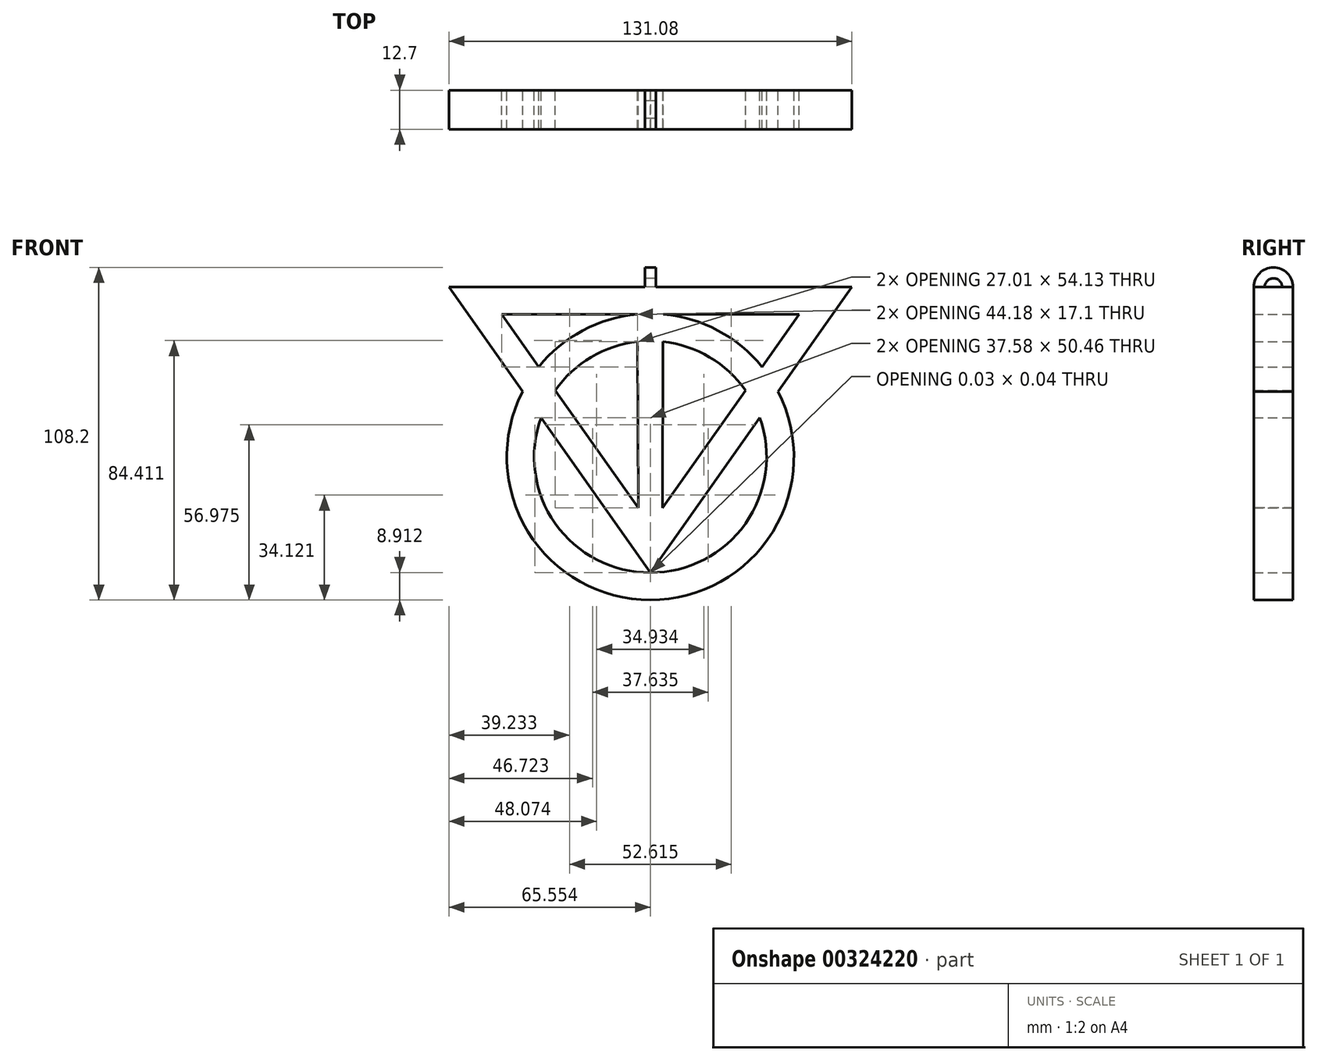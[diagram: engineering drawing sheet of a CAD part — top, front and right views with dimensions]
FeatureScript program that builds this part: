
annotation { "Feature Type Name" : "Feature", "Feature Type Description" : "" }
export const myFeature = defineFeature(function(context is Context, id is Id, definition is map)
    precondition{}
    {
        {
            var Q0;
            Q0=qCreatedBy(makeId("Front.planeOp"),FACE);
            var sketch = newSketch(context, id + "F0", { "sketchPlane" : qUnion([Q0])});
            skLineSegment(sketch, "E0", {"start": v(0.92, -47.6) * mm, "end": v(0.9, -47.56) * mm});
            skArc(sketch, "E1.trimOffspring", {"start": v(-2.73, 27.57) * mm, "mid": v(-2.98, 27.55) * mm, "end": v(-3.24, 27.52) * mm});
            skLineSegment(sketch, "E2.0", {"start": v(-2.9, -26.56) * mm, "end": v(-3.07, -26.3) * mm});
            skLineSegment(sketch, "E3.MirrorCS", {"start": v(0.92, -47.6) * mm, "end": v(36.48, 2.86) * mm});
            skLineSegment(sketch, "E4.MirrorCS", {"start": v(31.86, 11.74) * mm, "end": v(31.86, 11.74) * mm});
            skLineSegment(sketch, "E5.MirrorCS", {"start": v(37.24, 19.37) * mm, "end": v(49.29, 36.47) * mm});
            skLineSegment(sketch, "E6.trimOffspring", {"start": v(4.85, -26.58) * mm, "end": v(31.86, 11.74) * mm});
            skPoint(sketch, "E7.orphan", {"position": v(0.96, -32.1) * mm});
            skArc(sketch, "E8.trimOffspring", {"start": v(36.48, 2.86) * mm, "mid": v(31.83, -31.62) * mm, "end": v(0.92, -47.6) * mm});
            skArc(sketch, "E9.trimOffspring", {"start": v(0.86, -47.6) * mm, "mid": v(0.9, -47.6) * mm, "end": v(0.92, -47.6) * mm});
            skArc(sketch, "E10.0", {"start": v(0.86, -56.49) * mm, "mid": v(0.87, -56.49) * mm, "end": v(0.9, -56.49) * mm});
            skArc(sketch, "E11.0", {"start": v(42.46, 11.35) * mm, "mid": v(40.74, -34.25) * mm, "end": v(0.9, -56.49) * mm});
            skArc(sketch, "E12.0", {"start": v(5.1, 36.47) * mm, "mid": v(22.91, 31.19) * mm, "end": v(37.24, 19.37) * mm});
            skPoint(sketch, "E13.center.orphan", {"position": v(0.92, 32.3) * mm});
            skLineSegment(sketch, "E14", {"start": v(49.29, 36.47) * mm, "end": v(5.1, 36.47) * mm});
            skLineSegment(sketch, "E15.0", {"start": v(66.43, 45.36) * mm, "end": v(0.9, 45.36) * mm});
            skArc(sketch, "E16.0", {"start": v(5.02, 27.55) * mm, "mid": v(20.15, 22.55) * mm, "end": v(31.86, 11.74) * mm});
            skLineSegment(sketch, "E17", {"start": v(4.85, -26.58) * mm, "end": v(5.02, 27.55) * mm});
            skLineSegment(sketch, "E18.trimOffspring", {"start": v(42.46, 11.35) * mm, "end": v(66.43, 45.36) * mm});
            skLineSegment(sketch, "E19.trimOffspring", {"start": v(-3.04, 36.47) * mm, "end": v(-3.33, 36.47) * mm});
            skLineSegment(sketch, "E20", {"start": v(0.9, -47.6) * mm, "end": v(0.9, -47.56) * mm});
            skLineSegment(sketch, "E21.MirrorCS", {"start": v(-47.5, 36.47) * mm, "end": v(-46.74, 36.47) * mm});
            skLineSegment(sketch, "E22.MirrorCS", {"start": v(-3.07, -26.58) * mm, "end": v(-3.07, -26.3) * mm});
            skLineSegment(sketch, "E23.trimOffspring", {"start": v(0.9, 45.36) * mm, "end": v(65.54, 45.36) * mm});
            skPoint(sketch, "E24.MirrorCS.end.orphan", {"position": v(-3.07, -26.58) * mm});
            skPoint(sketch, "E24.MirrorCS.start.orphan", {"position": v(-30.08, 11.74) * mm});
            skPoint(sketch, "E25.MirrorCS.end.orphan", {"position": v(-64.65, 45.36) * mm});
            skPoint(sketch, "E25.MirrorCS.start.orphan", {"position": v(-40.68, 11.35) * mm});
            skPoint(sketch, "E26.MirrorCS.end.orphan", {"position": v(-63.76, 45.36) * mm});
            skPoint(sketch, "E27.orphan", {"position": v(-3.33, 36.47) * mm});
            skPoint(sketch, "E28.MirrorCS.start.orphan", {"position": v(-3.24, 27.55) * mm});
            skPoint(sketch, "E29.MirrorCS.start.orphan", {"position": v(-34.7, 2.86) * mm});
            skLineSegment(sketch, "E30.trimOffspring", {"start": v(-3.24, 27.52) * mm, "end": v(-3.24, 27.55) * mm});
            skArc(sketch, "E31.MirrorCS", {"start": v(-34.7, 2.86) * mm, "mid": v(-30.05, -31.62) * mm, "end": v(0.86, -47.6) * mm});
            skLineSegment(sketch, "E32.MirrorCS", {"start": v(0.86, -47.6) * mm, "end": v(-34.7, 2.86) * mm});
            skArc(sketch, "E33.MirrorCS", {"start": v(-40.68, 11.35) * mm, "mid": v(-38.96, -34.25) * mm, "end": v(0.9, -56.49) * mm});
            skLineSegment(sketch, "E34.MirrorCS", {"start": v(-3.07, -26.58) * mm, "end": v(-30.08, 11.74) * mm});
            skArc(sketch, "E35.MirrorCS", {"start": v(-3.24, 27.55) * mm, "mid": v(-18.37, 22.55) * mm, "end": v(-30.08, 11.74) * mm});
            skLineSegment(sketch, "E36.MirrorCS", {"start": v(-3.07, -26.58) * mm, "end": v(-3.24, 27.55) * mm});
            skArc(sketch, "E37.MirrorCS", {"start": v(-3.33, 36.47) * mm, "mid": v(-21.13, 31.19) * mm, "end": v(-35.45, 19.37) * mm});
            skLineSegment(sketch, "E38.MirrorCS", {"start": v(0.9, 45.36) * mm, "end": v(-64.65, 45.36) * mm});
            skLineSegment(sketch, "E39.MirrorCS", {"start": v(-40.68, 11.35) * mm, "end": v(-64.65, 45.36) * mm});
            skLineSegment(sketch, "E40.MirrorCS", {"start": v(-47.5, 36.47) * mm, "end": v(-3.33, 36.47) * mm});
            skLineSegment(sketch, "E41.MirrorCS", {"start": v(-35.45, 19.37) * mm, "end": v(-47.5, 36.47) * mm});
            skSolve(sketch);
        }
        {
            var Q0;
            {var subQ13=sQuery(id+"F0.wireOp",EDGE,"E0");Q0=makeQuery(id+"F0.imprint","IMPRINT",FACE,{"disambiguationData":[TD([[makeQuery(id+"F0.imprint","IMPRINT",EDGE,{"derivedFrom":subQ13}),-1.0]])]});}
            extrude(context, id + "F1", {"entities" : qUnion([Q0]), "depth" : 12.7 * mm});
        }
        {
            var Q0;
            Q0=makeQuery(id+"F1.opExtrude","SWEPT_FACE",FACE,{"disambiguationData":[OSD([sQuery(id+"F0.wireOp",EDGE,"E15.0"),sQuery(id+"F0.wireOp",EDGE,"E23.trimOffspring"),sQuery(id+"F0.wireOp",EDGE,"E38.MirrorCS")])]});
            var sketch = newSketch(context, id + "F2", { "sketchPlane" : qUnion([Q0])});
            skLineSegment(sketch, "E42.bottom", {"start": v(-0.9, 0) * mm, "end": v(2.7, 0) * mm});
            skLineSegment(sketch, "E42.top", {"start": v(-0.9, -3.52) * mm, "end": v(2.7, -3.52) * mm});
            skLineSegment(sketch, "E42.left", {"start": v(-0.9, 0) * mm, "end": v(-0.9, -3.52) * mm});
            skLineSegment(sketch, "E42.right", {"start": v(2.7, 0) * mm, "end": v(2.7, -3.52) * mm});
            skLineSegment(sketch, "E43", {"start": v(-8.1, -6.35) * mm, "end": v(8.6, -6.35) * mm});
            skSolve(sketch);
        }
        {
            var Q0;
            Q0=makeQuery(id+"F2.imprint","IMPRINT",FACE,{"disambiguationData":[TD([[makeQuery(id+"F2.imprint","IMPRINT",EDGE,{"derivedFrom":sQuery(id+"F2.wireOp",EDGE,"E42.bottom")}),1.0]])]});
            var Q1;
            Q1=sQuery(id+"F2.wireOp",EDGE,"E43");
            revolve(context, id + "F3", {"operationType" : NewBodyOperationType.ADD, "entities" : qUnion([Q0]), "axis" : qUnion([Q1]), "revolveType" : RevolveType.FULL});
        }
    });
